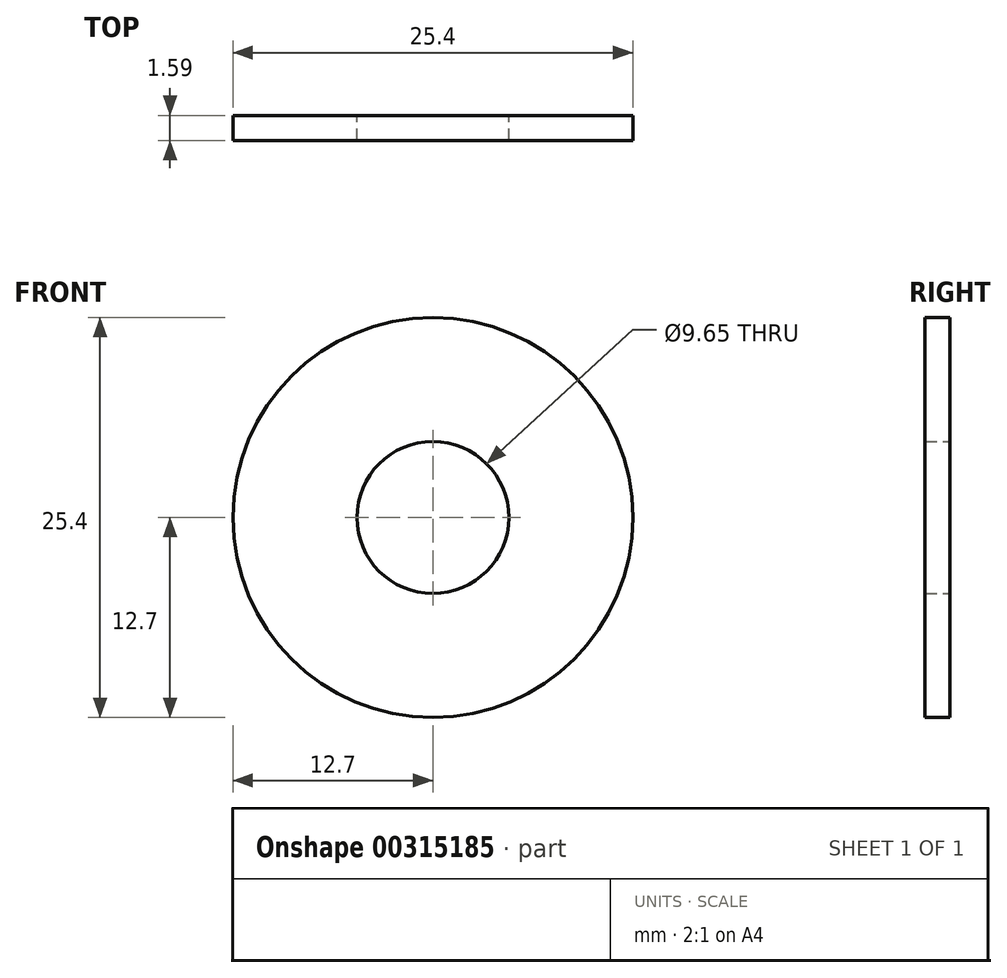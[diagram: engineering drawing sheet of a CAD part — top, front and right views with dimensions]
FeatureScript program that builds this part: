
annotation { "Feature Type Name" : "Feature", "Feature Type Description" : "" }
export const myFeature = defineFeature(function(context is Context, id is Id, definition is map)
    precondition{}
    {
        {
            var Q0;
            Q0=qCreatedBy(makeId("Front.planeOp"),FACE);
            var sketch = newSketch(context, id + "F0", { "sketchPlane" : qUnion([Q0])});
            skCircle(sketch, "E0", {"center": v(0, 0) * mm, "radius": 12.7 * mm});
            skCircle(sketch, "E1", {"center": v(0, 0) * mm, "radius": 4.83 * mm});
            skSolve(sketch);
        }
        {
            var Q0;
            Q0 = qSketchRegion(id + "F0", true);
            extrude(context, id + "F1", {"entities" : qUnion([Q0]), "depth" : 1.59 * mm});
        }
    });
